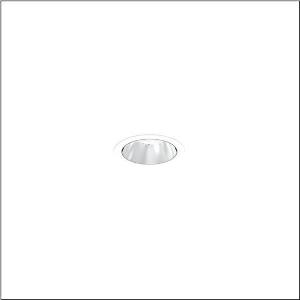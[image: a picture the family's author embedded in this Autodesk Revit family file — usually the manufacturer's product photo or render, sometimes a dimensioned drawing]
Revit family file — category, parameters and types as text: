
# Revit family: lunis_21_s_51db15ea91c
name_source: partatom
category: Lighting Fixtures
units: mm (PartAtom-declared; Revit-internal decimal feet)

## family parameters
Cut with Voids When Loaded = No
Host = Face
Light Source = No
Part Type = Normal
Room Calculation Point = No
Round Connector Dimension = Use Diameter
Shared = No

## types (1)
- --- (1 x LED, 1260 lm, 8 W, 4000K)
    Apparent Load = 8 VA
    CIE Flux Codes = 95 100 100 100 100
    Color Rendering = 80
    Color Temperature = 4000K
    Default Elevation = 1800 mm
    Description = Lunis 21,  S, downlight, light control with lens, of PMMA, anti glare with reflector, of PC, highly specular, light emission: direct distribution, LED rated luminous flux: 960lm, light colour: 830/840/865, with terminal, 5-pole, mains connection: 220..240V, AC, 50..60Hz, housing, round, of diecast aluminium, traffic white (RAL 9016), diameter: 84mm, clamping range: 1..40mm, protection rating (complete): IP20, protection rating (on room side): IP54, insulation class (complete): insulation class II (safety insulation), certification: CE, impact resistance: IK03, packaging unit: 1 piece
    Height = 0 mm  [stored 0 ft]
    Lamp = 1 x LED
    Lamp Light Flux = 1260 lm
    Lamp Power = 8 W
    Lamp count = 1
    Length = 84 mm
    Luminous efficacy = 158 lm/W
    Manufacturer = Siteco
    ModVariant = No
    Model = 51DB15EA91C
    Mounting Place = Ceiling
    Mounting Type = Recessed
    Number of Poles = 1
    OnlyDefault = Yes
    Power Factor = 1
    Product Name = Lunis 21 S
    Product group = downlight
    ProductGroupID = 400
    Protection Class = Protection class II
    Protection Degree = IP 20
    RLX_Detail_Level = 1
    RLX_Emergency_Light_Flux = 0 lm
    RLX_Emergency_Type = 0
    RLX_Emergency_Type_DB = No
    RlxData = <blob elided: 8461 chars, md5=31fb0e1c>
    Socket = socket
    Standby Power = 0 W
    System Light Flux = 1260 lm
    System Power = 8 W
    Type Comments = individual setting: colour temperature 4000K, luminous flux: 100 % | (OFF | OFF | ON | OFF) | 200 mA
    Type Image = l_1290840.jpg
    URL = http://relux.com
    VarID = @adj_017895
    Voltage = 0 V
    Weight = 0.00 kg
    Width = 0 mm  [stored 0 ft]

note: [stored X ft] marks values corroborated as IEEE doubles in the binary element streams (Revit-internal decimal feet)

## geometry (parser evidence)
native form markers: Sweep x9
no freeform markers — native parametric forms only
